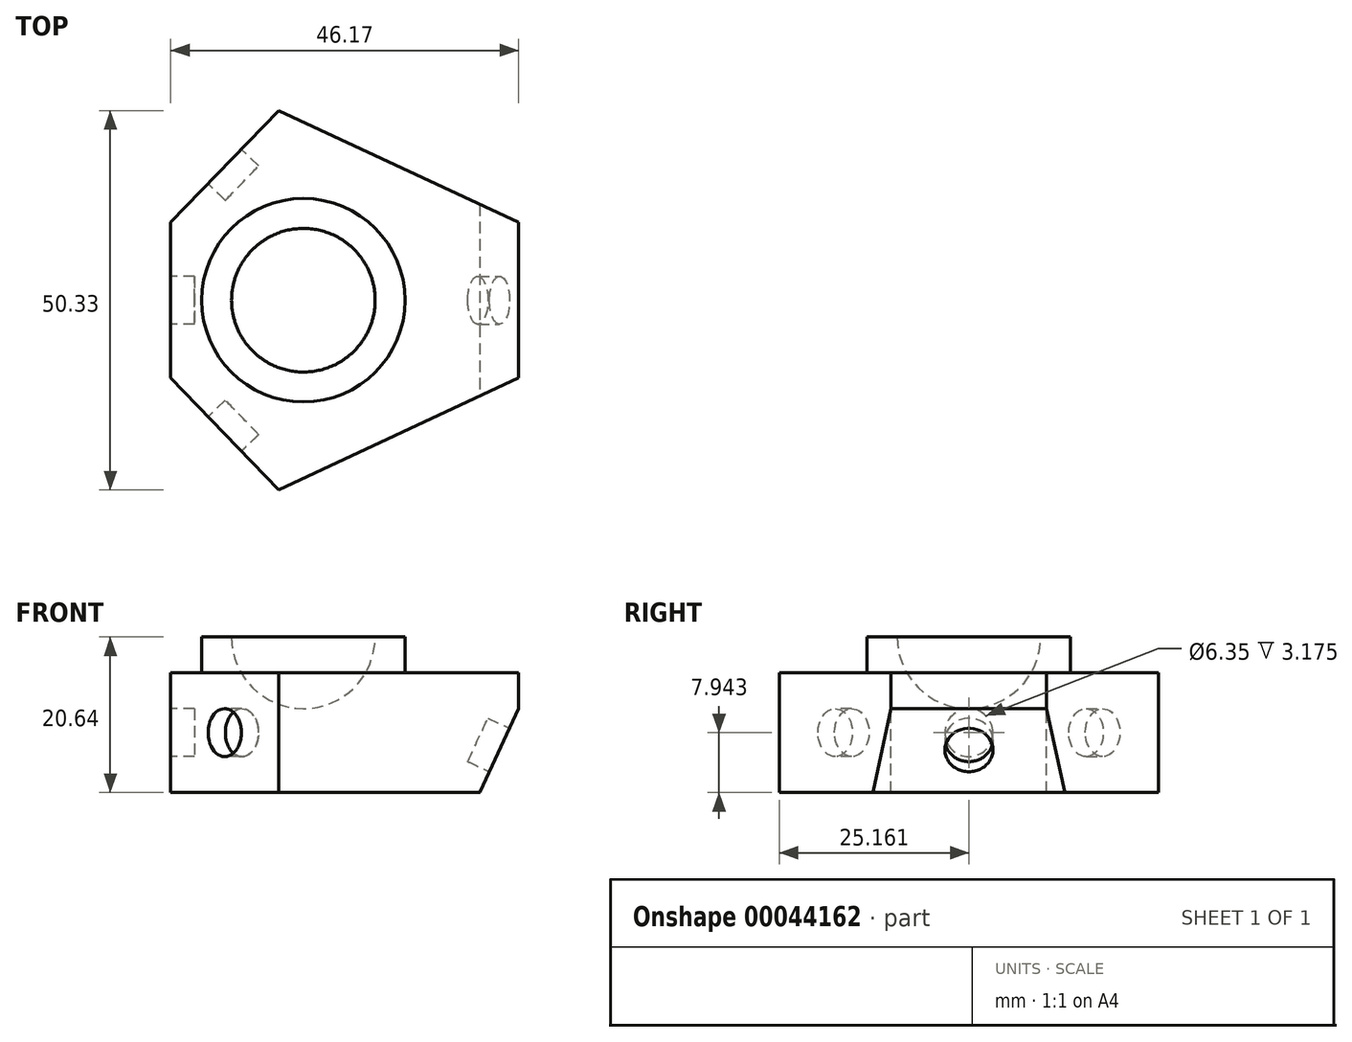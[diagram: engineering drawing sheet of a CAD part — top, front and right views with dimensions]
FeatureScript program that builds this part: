
annotation { "Feature Type Name" : "Feature", "Feature Type Description" : "" }
export const myFeature = defineFeature(function(context is Context, id is Id, definition is map)
    precondition{}
    {
        {
            var Q0;
            Q0=qCreatedBy(makeId("Top.planeOp"),FACE);
            var sketch = newSketch(context, id + "F0", { "sketchPlane" : qUnion([Q0])});
            skLineSegment(sketch, "E0", {"start": v(0, 0) * mm, "end": v(-31.84, 14.85) * mm});
            skLineSegment(sketch, "E1", {"start": v(-31.84, 14.85) * mm, "end": v(-46.17, 0) * mm});
            skLineSegment(sketch, "E2", {"start": v(-46.17, 0) * mm, "end": v(-46.17, -20.64) * mm});
            skLineSegment(sketch, "E3", {"start": v(-46.17, -20.64) * mm, "end": v(-31.84, -35.48) * mm});
            skLineSegment(sketch, "E4", {"start": v(-31.84, -35.48) * mm, "end": v(0, -20.64) * mm});
            skLineSegment(sketch, "E5", {"start": v(0, -20.64) * mm, "end": v(0, 0) * mm});
            skSolve(sketch);
        }
        {
            var Q0;
            Q0 = qSketchRegion(id + "F0", true);
            extrude(context, id + "F1", {"entities" : qUnion([Q0]), "oppositeDirection" : true, "depth" : 15.88 * mm});
        }
        {
            var Q0;
            Q0=qCreatedBy(makeId("Front.planeOp"),FACE);
            cPlane(context, id + "F2", {"entities" : qUnion([Q0]), "cplaneType" : CPlaneType.OFFSET, "offset" : 10.32 * mm, "width" : 152.4 * mm, "height" : 152.4 * mm});
        }
        {
            var Q0;
            Q0=makeQuery(id+"F1.opExtrude","CAP_FACE",FACE,{"disambiguationData":[OSD([sQuery(id+"F0.wireOp",EDGE,"E0"),sQuery(id+"F0.wireOp",EDGE,"E1"),sQuery(id+"F0.wireOp",EDGE,"E2"),sQuery(id+"F0.wireOp",EDGE,"E3"),sQuery(id+"F0.wireOp",EDGE,"E4"),sQuery(id+"F0.wireOp",EDGE,"E5")])],"isStart":true});
            var sketch = newSketch(context, id + "F3", { "sketchPlane" : qUnion([Q0])});
            skLineSegment(sketch, "E6", {"start": v(0, -10.32) * mm, "end": v(-28.58, -10.32) * mm});
            skPoint(sketch, "E6.endSnap0", {"position": v(0, -10.32) * mm});
            skCircle(sketch, "E7", {"center": v(-28.58, -10.32) * mm, "radius": 13.5 * mm});
            skSolve(sketch);
        }
        {
            var Q0;
            Q0 = qSketchRegion(id + "F3", true);
            extrude(context, id + "F4", {"entities" : qUnion([Q0]), "operationType" : NewBodyOperationType.ADD, "depth" : 4.76 * mm});
        }
        {
            var Q0;
            Q0=qCreatedBy(id+"F2.planeOp",FACE);
            var sketch = newSketch(context, id + "F5", { "sketchPlane" : qUnion([Q0])});
            skLineSegment(sketch, "E8", {"start": v(0, 0) * mm, "end": v(-28.58, 0) * mm});
            skLineSegment(sketch, "E9", {"start": v(-28.58, 0) * mm, "end": v(-28.58, 4.77) * mm});
            skLineSegment(sketch, "E10", {"start": v(-28.58, 4.77) * mm, "end": v(-19.05, 4.77) * mm});
            skArc(sketch, "E11", {"start": v(-19.05, 4.77) * mm, "mid": v(-28.58, -4.75) * mm, "end": v(-38.1, 4.77) * mm});
            skLineSegment(sketch, "E12", {"start": v(-28.58, 4.77) * mm, "end": v(-38.1, 4.77) * mm});
            skSolve(sketch);
        }
        {
            var Q0;
            Q0 = qSketchRegion(id + "F5", true);
            var Q1;
            Q1=sQuery(id+"F5.wireOp",EDGE,"E10");
            revolve(context, id + "F6", {"operationType" : NewBodyOperationType.REMOVE, "entities" : qUnion([Q0]), "axis" : qUnion([Q1]), "revolveType" : RevolveType.FULL, "oppositeDirection" : true});
        }
        {
            var Q0;
            Q0=makeQuery(id+"F1.opExtrude","SWEPT_FACE",FACE,{"disambiguationData":[OSD([sQuery(id+"F0.wireOp",EDGE,"E3")])]});
            var sketch = newSketch(context, id + "F7", { "sketchPlane" : qUnion([Q0])});
            skCircle(sketch, "E13", {"center": v(-6.9, -7.94) * mm, "radius": 3.18 * mm});
            skPoint(sketch, "E13.centerSnap0", {"position": v(-6.9, -15.88) * mm});
            skPoint(sketch, "E13.centerSnap1", {"position": v(-17.23, -7.94) * mm});
            skSolve(sketch);
        }
        {
            var Q0;
            Q0 = qSketchRegion(id + "F7", true);
            extrude(context, id + "F8", {"entities" : qUnion([Q0]), "operationType" : NewBodyOperationType.REMOVE, "oppositeDirection" : true, "depth" : 3.17 * mm});
        }
        {
            var Q0;
            Q0=makeQuery(id+"F1.opExtrude","SWEPT_FACE",FACE,{"disambiguationData":[OSD([sQuery(id+"F0.wireOp",EDGE,"E2")])]});
            var sketch = newSketch(context, id + "F9", { "sketchPlane" : qUnion([Q0])});
            skCircle(sketch, "E14", {"center": v(10.32, -7.94) * mm, "radius": 3.18 * mm});
            skPoint(sketch, "E14.centerSnap0", {"position": v(0, -7.94) * mm});
            skPoint(sketch, "E14.centerSnap1", {"position": v(10.32, -15.88) * mm});
            skSolve(sketch);
        }
        {
            var Q0;
            Q0 = qSketchRegion(id + "F9", true);
            extrude(context, id + "F10", {"entities" : qUnion([Q0]), "operationType" : NewBodyOperationType.REMOVE, "oppositeDirection" : true, "depth" : 3.17 * mm});
        }
        {
            var Q0;
            Q0=makeQuery(id+"F1.opExtrude","SWEPT_FACE",FACE,{"disambiguationData":[OSD([sQuery(id+"F0.wireOp",EDGE,"E1")])]});
            var sketch = newSketch(context, id + "F11", { "sketchPlane" : qUnion([Q0])});
            skCircle(sketch, "E15", {"center": v(21.76, -7.94) * mm, "radius": 3.18 * mm});
            skPoint(sketch, "E15.centerSnap0", {"position": v(21.76, -15.88) * mm});
            skPoint(sketch, "E15.centerSnap1", {"position": v(11.44, -7.94) * mm});
            skSolve(sketch);
        }
        {
            var Q0;
            Q0 = qSketchRegion(id + "F11", true);
            extrude(context, id + "F12", {"entities" : qUnion([Q0]), "operationType" : NewBodyOperationType.REMOVE, "oppositeDirection" : true, "depth" : 3.17 * mm});
        }
        {
            var Q0;
            Q0=qCreatedBy(id+"F2.planeOp",FACE);
            var sketch = newSketch(context, id + "F13", { "sketchPlane" : qUnion([Q0])});
            skLineSegment(sketch, "E16", {"start": v(0, 0) * mm, "end": v(0, -4.76) * mm});
            skLineSegment(sketch, "E17", {"start": v(0, -4.76) * mm, "end": v(-5.18, -15.88) * mm});
            skLineSegment(sketch, "E18", {"start": v(-5.18, -15.88) * mm, "end": v(0, -15.88) * mm});
            skLineSegment(sketch, "E19", {"start": v(0, -15.88) * mm, "end": v(0, -4.76) * mm});
            skSolve(sketch);
        }
        {
            var Q0;
            Q0 = qSketchRegion(id + "F13", true);
            extrude(context, id + "F14", {"entities" : qUnion([Q0]), "operationType" : NewBodyOperationType.REMOVE, "endBound" : BoundingType.SYMMETRIC, "oppositeDirection" : true, "depth" : 25.4 * mm});
        }
        {
            var Q0;
            Q0=makeQuery(id+"F14.boolean.opBoolean","COPY",FACE,{"derivedFrom":makeQuery(id+"F14.opExtrude","SWEPT_FACE",FACE,{"disambiguationData":[OSD([sQuery(id+"F13.wireOp",EDGE,"E17")])]})});
            var sketch = newSketch(context, id + "F15", { "sketchPlane" : qUnion([Q0])});
            skCircle(sketch, "E20", {"center": v(-10.32, -10.36) * mm, "radius": 3.18 * mm});
            skPoint(sketch, "E20.centerSnap0", {"position": v(1.2, -10.36) * mm});
            skPoint(sketch, "E20.centerSnap1", {"position": v(-10.32, -4.32) * mm});
            skSolve(sketch);
        }
        {
            var Q0;
            Q0 = qSketchRegion(id + "F15", true);
            extrude(context, id + "F16", {"entities" : qUnion([Q0]), "operationType" : NewBodyOperationType.REMOVE, "oppositeDirection" : true, "depth" : 3.17 * mm});
        }
    });
